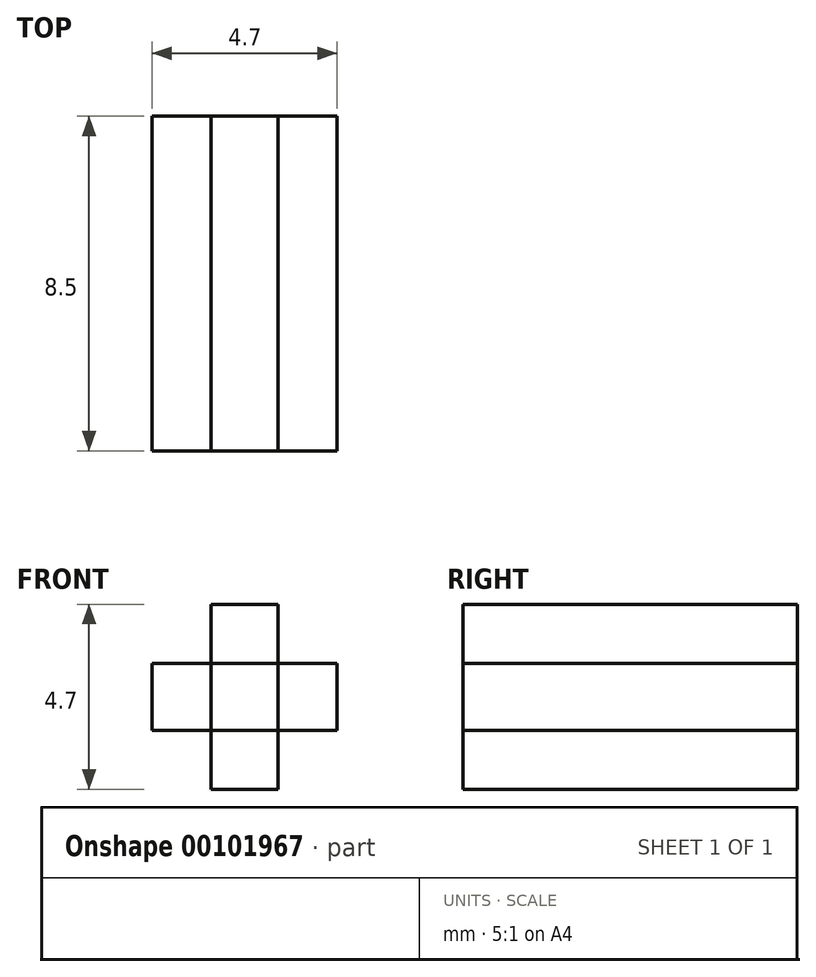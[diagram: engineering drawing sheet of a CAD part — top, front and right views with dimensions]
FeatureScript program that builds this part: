
annotation { "Feature Type Name" : "Feature", "Feature Type Description" : "" }
export const myFeature = defineFeature(function(context is Context, id is Id, definition is map)
    precondition{}
    {
        {
            var Q0;
            Q0=qCreatedBy(makeId("Front.planeOp"),FACE);
            var sketch = newSketch(context, id + "F0", { "sketchPlane" : qUnion([Q0])});
            skLineSegment(sketch, "E0.bottom", {"start": v(0.85, 2.35) * mm, "end": v(-0.85, 2.35) * mm});
            skLineSegment(sketch, "E0.top", {"start": v(0.85, -2.35) * mm, "end": v(-0.85, -2.35) * mm});
            skLineSegment(sketch, "E0.left", {"start": v(0.85, 2.35) * mm, "end": v(0.85, -2.35) * mm});
            skLineSegment(sketch, "E0.right", {"start": v(-0.85, 2.35) * mm, "end": v(-0.85, -2.35) * mm});
            skPoint(sketch, "E0.middle", {"position": v(0, 0) * mm});
            skSolve(sketch);
        }
        {
            var Q0;
            Q0=qCreatedBy(makeId("Front.planeOp"),FACE);
            var sketch = newSketch(context, id + "F1", { "sketchPlane" : qUnion([Q0])});
            skLineSegment(sketch, "E1.bottom", {"start": v(2.35, 0.85) * mm, "end": v(-2.35, 0.85) * mm});
            skLineSegment(sketch, "E1.top", {"start": v(2.35, -0.85) * mm, "end": v(-2.35, -0.85) * mm});
            skLineSegment(sketch, "E1.left", {"start": v(2.35, 0.85) * mm, "end": v(2.35, -0.85) * mm});
            skLineSegment(sketch, "E1.right", {"start": v(-2.35, 0.85) * mm, "end": v(-2.35, -0.85) * mm});
            skPoint(sketch, "E1.middle", {"position": v(0, 0) * mm});
            skSolve(sketch);
        }
        {
            var Q0;
            Q0=makeQuery(id+"F0.imprint","IMPRINT",FACE,{"disambiguationData":[TD([[makeQuery(id+"F0.imprint","IMPRINT",EDGE,{"derivedFrom":sQuery(id+"F0.wireOp",EDGE,"E0.bottom")}),1.0]])]});
            var Q1;
            Q1=makeQuery(id+"F1.imprint","IMPRINT",FACE,{"disambiguationData":[TD([[makeQuery(id+"F1.imprint","IMPRINT",EDGE,{"derivedFrom":sQuery(id+"F1.wireOp",EDGE,"E1.bottom")}),1.0]])]});
            extrude(context, id + "F2", {"entities" : qUnion([Q0, Q1]), "depth" : 8.5 * mm});
        }
    });
